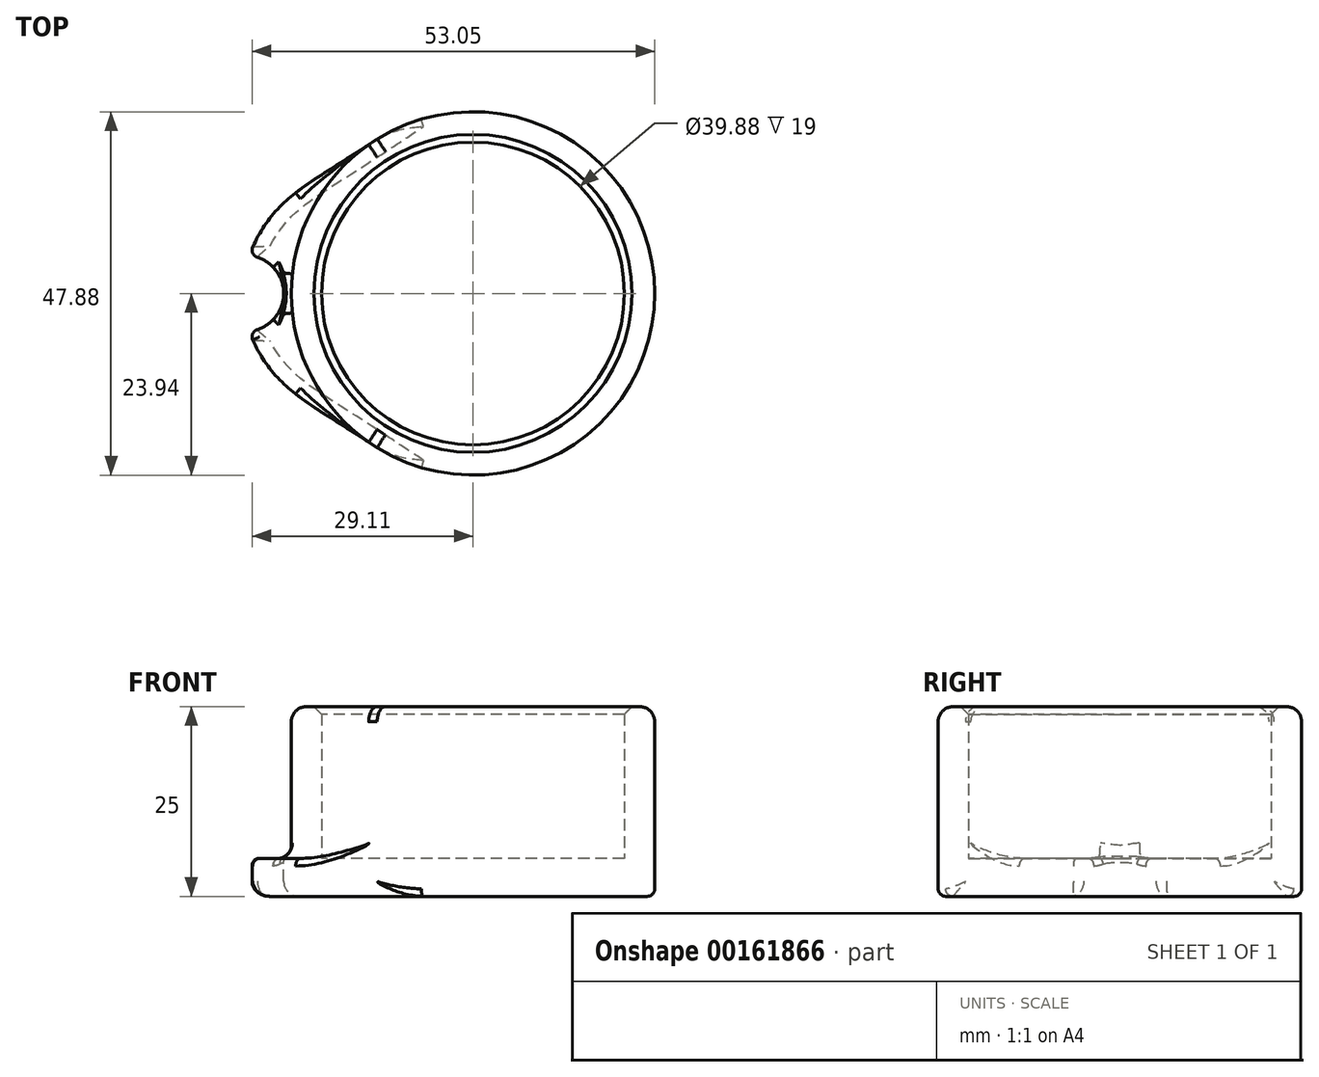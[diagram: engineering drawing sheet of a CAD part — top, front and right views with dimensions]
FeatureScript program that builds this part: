
annotation { "Feature Type Name" : "Feature", "Feature Type Description" : "" }
export const myFeature = defineFeature(function(context is Context, id is Id, definition is map)
    precondition{}
    {
        {
            var Q0;
            Q0=qCreatedBy(makeId("Top.planeOp"),FACE);
            var sketch = newSketch(context, id + "F0", { "sketchPlane" : qUnion([Q0])});
            skCircle(sketch, "E0", {"center": v(0, 0) * mm, "radius": 19.94 * mm});
            skCircle(sketch, "E1.0", {"center": v(0, 0) * mm, "radius": 23.94 * mm});
            skLineSegment(sketch, "E2", {"start": v(0, 0) * mm, "end": v(-70.93, 0) * mm, "construction": true});
            skArc(sketch, "E3.MirrorCS", {"start": v(-24.94, 0) * mm, "mid": v(-25.9, 2.95) * mm, "end": v(-28.42, 4.76) * mm});
            skFitSpline(sketch, "E4", {"points": [v(-29.52, 4.98) * mm, v(-12.62, 20.34) * mm], "startDerivative": vector(9.52, 23.06) * mm, "endDerivative": vector(29.52, 19.63) * mm});
            skArc(sketch, "E5.filletArc", {"start": v(-29.02, 6.14) * mm, "mid": v(-29.03, 5.31) * mm, "end": v(-28.42, 4.76) * mm});
            skFitSpline(sketch, "E6.MirrorCS", {"points": [v(-29.52, -4.98) * mm, v(-12.62, -20.34) * mm], "startDerivative": vector(9.52, -23.06) * mm, "endDerivative": vector(29.52, -19.63) * mm});
            skArc(sketch, "E7.MirrorCS", {"start": v(-24.94, 0) * mm, "mid": v(-25.9, -2.95) * mm, "end": v(-28.42, -4.76) * mm});
            skArc(sketch, "E8.MirrorCS", {"start": v(-29.02, -6.14) * mm, "mid": v(-29.03, -5.31) * mm, "end": v(-28.42, -4.76) * mm});
            skSolve(sketch);
        }
        {
            var Q0;
            Q0=makeQuery(id+"F0.imprint","IMPRINT",FACE,{"disambiguationData":[TD([[makeQuery(id+"F0.imprint","IMPRINT",EDGE,{"derivedFrom":sQuery(id+"F0.wireOp",EDGE,"E0")}),-1.0]])]});
            extrude(context, id + "F1", {"entities" : qUnion([Q0]), "depth" : 20 * mm});
        }
        {
            var Q0;
            Q0=makeQuery(id+"F0.imprint","IMPRINT",FACE,{"disambiguationData":[TD([[makeQuery(id+"F0.imprint","IMPRINT",EDGE,{"derivedFrom":sQuery(id+"F0.wireOp",EDGE,"E1.0")}),-1.0]])]});
            var Q1;
            Q1=makeQuery(id+"F0.imprint","IMPRINT",FACE,{"disambiguationData":[TD([[makeQuery(id+"F0.imprint","IMPRINT",EDGE,{"derivedFrom":sQuery(id+"F0.wireOp",EDGE,"E0")}),-1.0]])]});
            var Q2;
            Q2=makeQuery(id+"F0.imprint","IMPRINT",FACE,{"disambiguationData":[TD([[makeQuery(id+"F0.imprint","IMPRINT",EDGE,{"derivedFrom":sQuery(id+"F0.wireOp",EDGE,"E0")}),1.0]])]});
            extrude(context, id + "F2", {"entities" : qUnion([Q0, Q1, Q2]), "operationType" : NewBodyOperationType.ADD, "oppositeDirection" : true, "depth" : 5 * mm});
        }
        {
            var Q0;
            Q0=makeQuery(id+"F1.opExtrude","CAP_EDGE",EDGE,{"disambiguationData":[OSD([sQuery(id+"F0.wireOp",EDGE,"E1.0")])],"isStart":true});
            var Q1;
            {var subQ0=sQuery(id+"F0.wireOp",EDGE,"E1.0");Q1=makeQuery(id+"F1.opExtrude","CAP_EDGE",EDGE,{"disambiguationData":[OSD([subQ0]),TDD([makeQuery(id+"F0.imprint","IMPRINT",EDGE,{"disambiguationData":[TD([[makeQuery(id+"F0.imprint","INTERSECT",VERTEX,{"disambiguationData":[OD(1.0)],"derivedFrom":[subQ0,sQuery(id+"F0.wireOp",EDGE,"E4")]}),-1.0]])],"derivedFrom":subQ0})])],"isStart":false});}
            var Q2;
            Q2=makeQuery(id+"F1.opExtrude","CAP_EDGE",EDGE,{"disambiguationData":[OSD([sQuery(id+"F0.wireOp",EDGE,"E6.MirrorCS")])],"isStart":false});
            var Q3;
            {var subQ0=sQuery(id+"F0.wireOp",EDGE,"E1.0");Q3=makeQuery(id+"F1.opExtrude","CAP_EDGE",EDGE,{"disambiguationData":[OSD([subQ0]),TDD([makeQuery(id+"F0.imprint","IMPRINT",EDGE,{"disambiguationData":[TD([[makeQuery(id+"F0.imprint","INTERSECT",VERTEX,{"disambiguationData":[OD(0.0)],"derivedFrom":[subQ0,sQuery(id+"F0.wireOp",EDGE,"E4")]}),1.0]])],"derivedFrom":subQ0})])],"isStart":false});}
            var Q4;
            Q4=makeQuery(id+"F1.opExtrude","CAP_EDGE",EDGE,{"disambiguationData":[OSD([sQuery(id+"F0.wireOp",EDGE,"E4")])],"isStart":false});
            var Q5;
            Q5=makeQuery(id+"F2.opExtrude","CAP_EDGE",EDGE,{"disambiguationData":[OSD([sQuery(id+"F0.wireOp",EDGE,"E3.MirrorCS"),sQuery(id+"F0.wireOp",EDGE,"E7.MirrorCS")])],"isStart":false});
            fillet(context, id + "F3", {"entities" : qUnion([Q0, Q1, Q2, Q3, Q4, Q5]), "radius" : 2 * mm, "tangentPropagation" : true, "allowEdgeOverflow" : false});
        }
        {
            var Q0;
            Q0=makeQuery(id+"F1.opExtrude","CAP_EDGE",EDGE,{"disambiguationData":[OSD([sQuery(id+"F0.wireOp",EDGE,"E0")])],"isStart":false});
            chamfer(context, id + "F4", {"entities" : qUnion([Q0]), "width" : 1 * mm, "tangentPropagation" : true});
        }
        {
            var Q0;
            Q0=makeQuery(id+"F1.opExtrude","CAP_EDGE",EDGE,{"disambiguationData":[OSD([sQuery(id+"F0.wireOp",EDGE,"E0")])],"isStart":true});
            var Q1;
            Q1=makeQuery(id+"F2.opExtrude","CAP_EDGE",EDGE,{"disambiguationData":[OSD([sQuery(id+"F0.wireOp",EDGE,"E4")])],"isStart":true});
            var Q2;
            Q2=makeQuery(id+"F2.opExtrude","CAP_EDGE",EDGE,{"disambiguationData":[OSD([sQuery(id+"F0.wireOp",EDGE,"E5.filletArc")])],"isStart":true});
            var Q3;
            Q3=makeQuery(id+"F2.opExtrude","CAP_EDGE",EDGE,{"disambiguationData":[OSD([sQuery(id+"F0.wireOp",EDGE,"E1.0")])],"isStart":false});
            fillet(context, id + "F5", {"entities" : qUnion([Q0, Q1, Q2, Q3]), "radius" : 1 * mm, "tangentPropagation" : true, "allowEdgeOverflow" : false});
        }
    });
